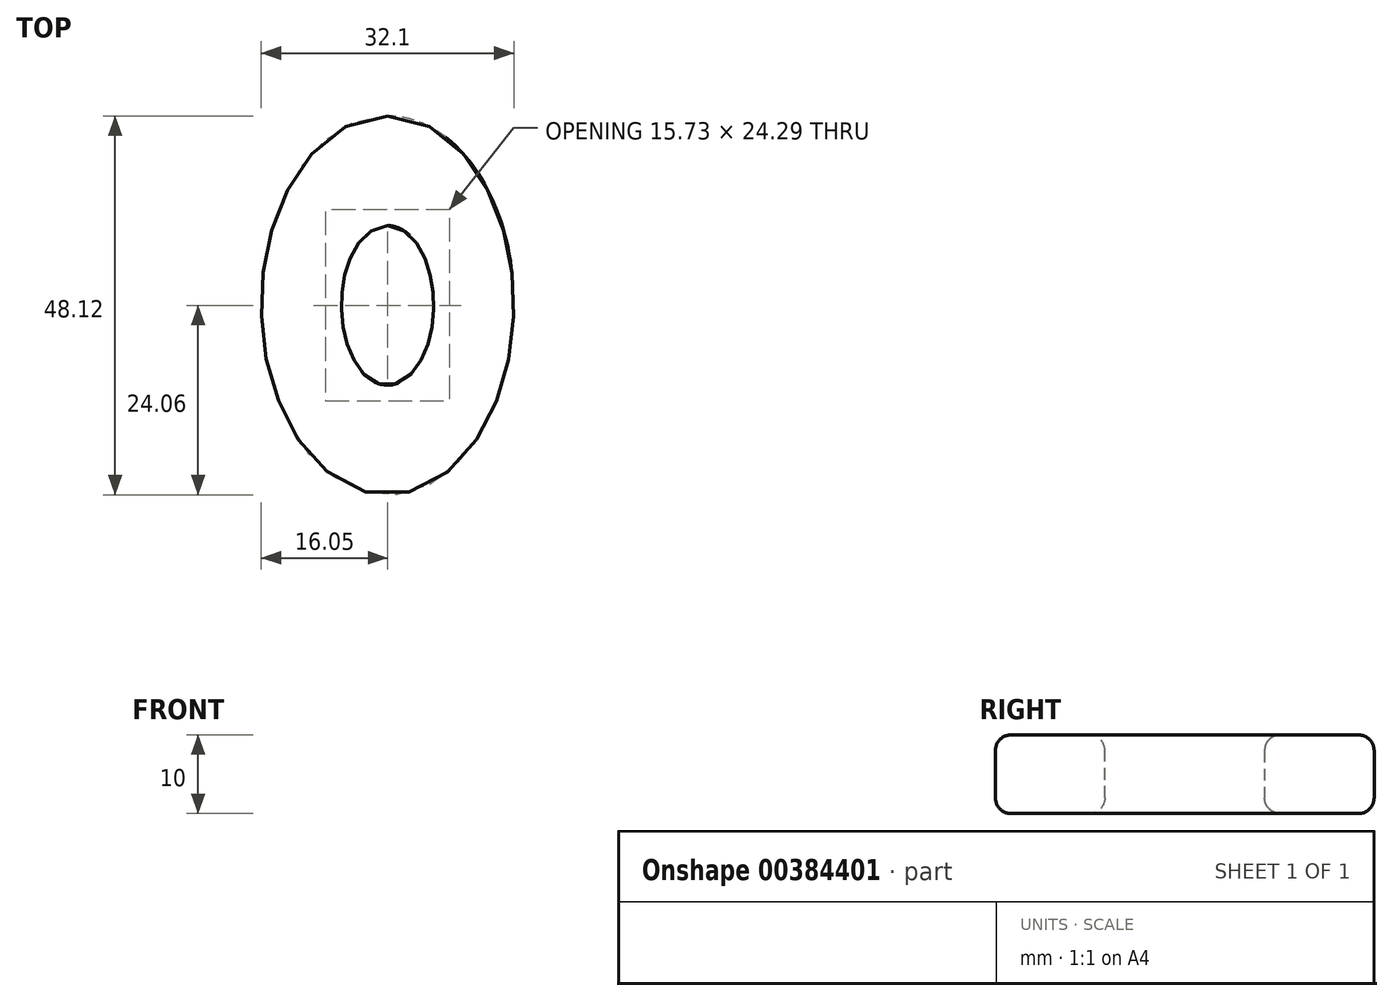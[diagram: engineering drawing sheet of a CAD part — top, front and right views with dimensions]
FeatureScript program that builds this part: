
annotation { "Feature Type Name" : "Feature", "Feature Type Description" : "" }
export const myFeature = defineFeature(function(context is Context, id is Id, definition is map)
    precondition{}
    {
        {
            var Q0;
            Q0=qCreatedBy(makeId("Top.planeOp"),FACE);
            var sketch = newSketch(context, id + "F0", { "sketchPlane" : qUnion([Q0])});
            skEllipse(sketch, "E0", {"center": v(0, 0) * mm, "majorRadius": 24.06 * mm, "minorRadius": 16.05 * mm, "majorAxis": v(0, 1)});
            skEllipse(sketch, "E1", {"center": v(0, 0) * mm, "majorRadius": 10.14 * mm, "minorRadius": 5.87 * mm, "majorAxis": v(0, 1)});
            skSolve(sketch);
        }
        {
            var Q0;
            Q0 = qSketchRegion(id + "F0", true);
            extrude(context, id + "F1", {"entities" : qUnion([Q0]), "depth" : 10 * mm});
        }
        {
            var Q0;
            Q0=makeQuery(id+"F1.opExtrude","CAP_FACE",FACE,{"disambiguationData":[OSD([sQuery(id+"F0.wireOp",EDGE,"E0"),sQuery(id+"F0.wireOp",EDGE,"E1")])],"isStart":false});
            fillet(context, id + "F2", {"entities" : qUnion([Q0]), "radius" : 2 * mm, "tangentPropagation" : true, "allowEdgeOverflow" : false});
        }
        {
            var Q0;
            Q0=makeQuery(id+"F1.opExtrude","CAP_FACE",FACE,{"disambiguationData":[OSD([sQuery(id+"F0.wireOp",EDGE,"E0"),sQuery(id+"F0.wireOp",EDGE,"E1")])],"isStart":true});
            var Q1;
            Q1=makeQuery(id+"F1.opExtrude","SWEPT_FACE",FACE,{"disambiguationData":[OSD([sQuery(id+"F0.wireOp",EDGE,"E1")])]});
            var Q2;
            Q2=makeQuery(id+"F1.opExtrude","SWEPT_FACE",FACE,{"disambiguationData":[OSD([sQuery(id+"F0.wireOp",EDGE,"E0")])]});
            var Q3;
            Q3=makeQuery(id+"F1.opExtrude","CAP_EDGE",EDGE,{"disambiguationData":[OSD([sQuery(id+"F0.wireOp",EDGE,"E1")])],"isStart":true});
            var Q4;
            {var subQ0=sQuery(id+"F0.wireOp",EDGE,"E0");Q4=makeQuery(id+"F2.opFillet","BLEND_EDGE",EDGE,{"blendedFrom":[makeQuery(id+"F1.opExtrude","CAP_EDGE",EDGE,{"disambiguationData":[OSD([subQ0])],"isStart":false}),makeQuery(id+"F1.opExtrude","CAP_FACE",FACE,{"disambiguationData":[OSD([subQ0,sQuery(id+"F0.wireOp",EDGE,"E1")])],"isStart":false})],"blendedInto":[makeQuery(id+"F1.opExtrude","CAP_FACE",FACE,{"disambiguationData":[OSD([subQ0,sQuery(id+"F0.wireOp",EDGE,"E1")])],"isStart":false})]});}
            var Q5;
            {var subQ0=sQuery(id+"F0.wireOp",EDGE,"E1");Q5=makeQuery(id+"F2.opFillet","BLEND_EDGE",EDGE,{"blendedFrom":[makeQuery(id+"F1.opExtrude","CAP_EDGE",EDGE,{"disambiguationData":[OSD([subQ0])],"isStart":false}),makeQuery(id+"F1.opExtrude","CAP_FACE",FACE,{"disambiguationData":[OSD([sQuery(id+"F0.wireOp",EDGE,"E0"),subQ0])],"isStart":false})],"blendedInto":[makeQuery(id+"F1.opExtrude","CAP_FACE",FACE,{"disambiguationData":[OSD([sQuery(id+"F0.wireOp",EDGE,"E0"),subQ0])],"isStart":false})]});}
            var Q6;
            Q6=makeQuery(id+"F2.opFillet","BLEND_FACE",FACE,{"disambiguationData":[OSD([sQuery(id+"F0.wireOp",EDGE,"E1")])]});
            var Q7;
            Q7=makeQuery(id+"F1.opExtrude","CAP_EDGE",EDGE,{"disambiguationData":[OSD([sQuery(id+"F0.wireOp",EDGE,"E0")])],"isStart":true});
            var Q8;
            {var subQ0=sQuery(id+"F0.wireOp",EDGE,"E0");Q8=makeQuery(id+"F2.opFillet","BLEND_EDGE",EDGE,{"blendedFrom":[makeQuery(id+"F1.opExtrude","CAP_EDGE",EDGE,{"disambiguationData":[OSD([subQ0])],"isStart":false}),makeQuery(id+"F1.opExtrude","SWEPT_FACE",FACE,{"disambiguationData":[OSD([subQ0])]})],"blendedInto":[makeQuery(id+"F1.opExtrude","SWEPT_FACE",FACE,{"disambiguationData":[OSD([subQ0])]})]});}
            var Q9;
            Q9=makeQuery(id+"F2.opFillet","BLEND_FACE",FACE,{"disambiguationData":[OSD([sQuery(id+"F0.wireOp",EDGE,"E0")])]});
            var Q10;
            Q10=makeQuery(id+"F1.opExtrude","CAP_FACE",FACE,{"disambiguationData":[OSD([sQuery(id+"F0.wireOp",EDGE,"E0"),sQuery(id+"F0.wireOp",EDGE,"E1")])],"isStart":false});
            var Q11;
            {var subQ0=sQuery(id+"F0.wireOp",EDGE,"E1");Q11=makeQuery(id+"F2.opFillet","BLEND_EDGE",EDGE,{"blendedFrom":[makeQuery(id+"F1.opExtrude","CAP_EDGE",EDGE,{"disambiguationData":[OSD([subQ0])],"isStart":false}),makeQuery(id+"F1.opExtrude","SWEPT_FACE",FACE,{"disambiguationData":[OSD([subQ0])]})],"blendedInto":[makeQuery(id+"F1.opExtrude","SWEPT_FACE",FACE,{"disambiguationData":[OSD([subQ0])]})]});}
            var Q12;
            Q12=makeQuery(id+"F1.opExtrude","CAP_FACE",FACE,{"disambiguationData":[OSD([sQuery(id+"F0.wireOp",EDGE,"E0"),sQuery(id+"F0.wireOp",EDGE,"E1")])],"isStart":true});
            fillet(context, id + "F3", {"entities" : qUnion([Q0, Q1, Q2, Q3, Q4, Q5, Q6, Q7, Q8, Q9, Q10, Q11, Q12]), "radius" : 2 * mm, "tangentPropagation" : true, "allowEdgeOverflow" : false});
        }
    });
